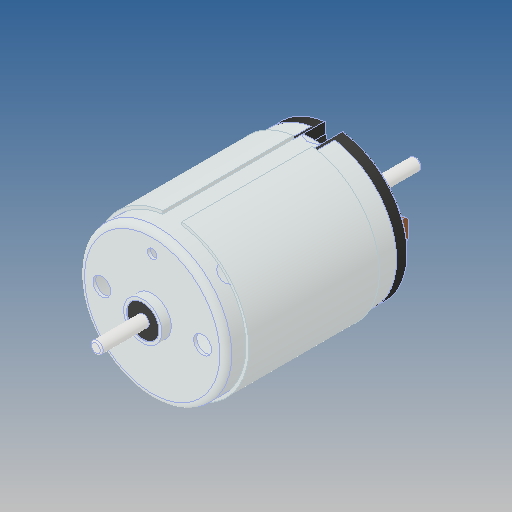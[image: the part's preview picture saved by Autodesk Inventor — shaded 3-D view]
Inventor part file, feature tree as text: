
AUTODESK INVENTOR PART (.ipt)
format: ipt  version: 2020 (Build 240168000, 168)  size: 348,672 bytes
history: mixed  units: mm
features: other x5, fillet x3, imported_body x1
ambient origin geometry x8: Origin, YZ Plane, XZ Plane, XY Plane, X Axis, Y Axis, Z Axis, Center Point
bodies: Body1 (imported_parasolid), Body2 (imported_parasolid), Body3 (imported_parasolid), Body4 (imported_parasolid)
feature tree (9):
  other  "Твердое тело1"
  other  "Твердое тело2"
  other  "Твердое тело3"
  other  "Твердое тело4"
  other  "Cut-Extrude8"
  fillet  "Fillet5"  [1 undecoded]
  fillet  "Fillet6"  [1 undecoded]
  fillet  "Fillet7"  [1 undecoded]
  imported_body  NMx_Import_Brep_tag  [imported B-rep: ~49 faces, bbox_mm=[20.9, 14.800391, 54.0]]
note: 3 required parameter values undecoded (feature->parameter linkage not recoverable at this tier; creation-order binding heuristic only, values carry confidence <= 0.55)
